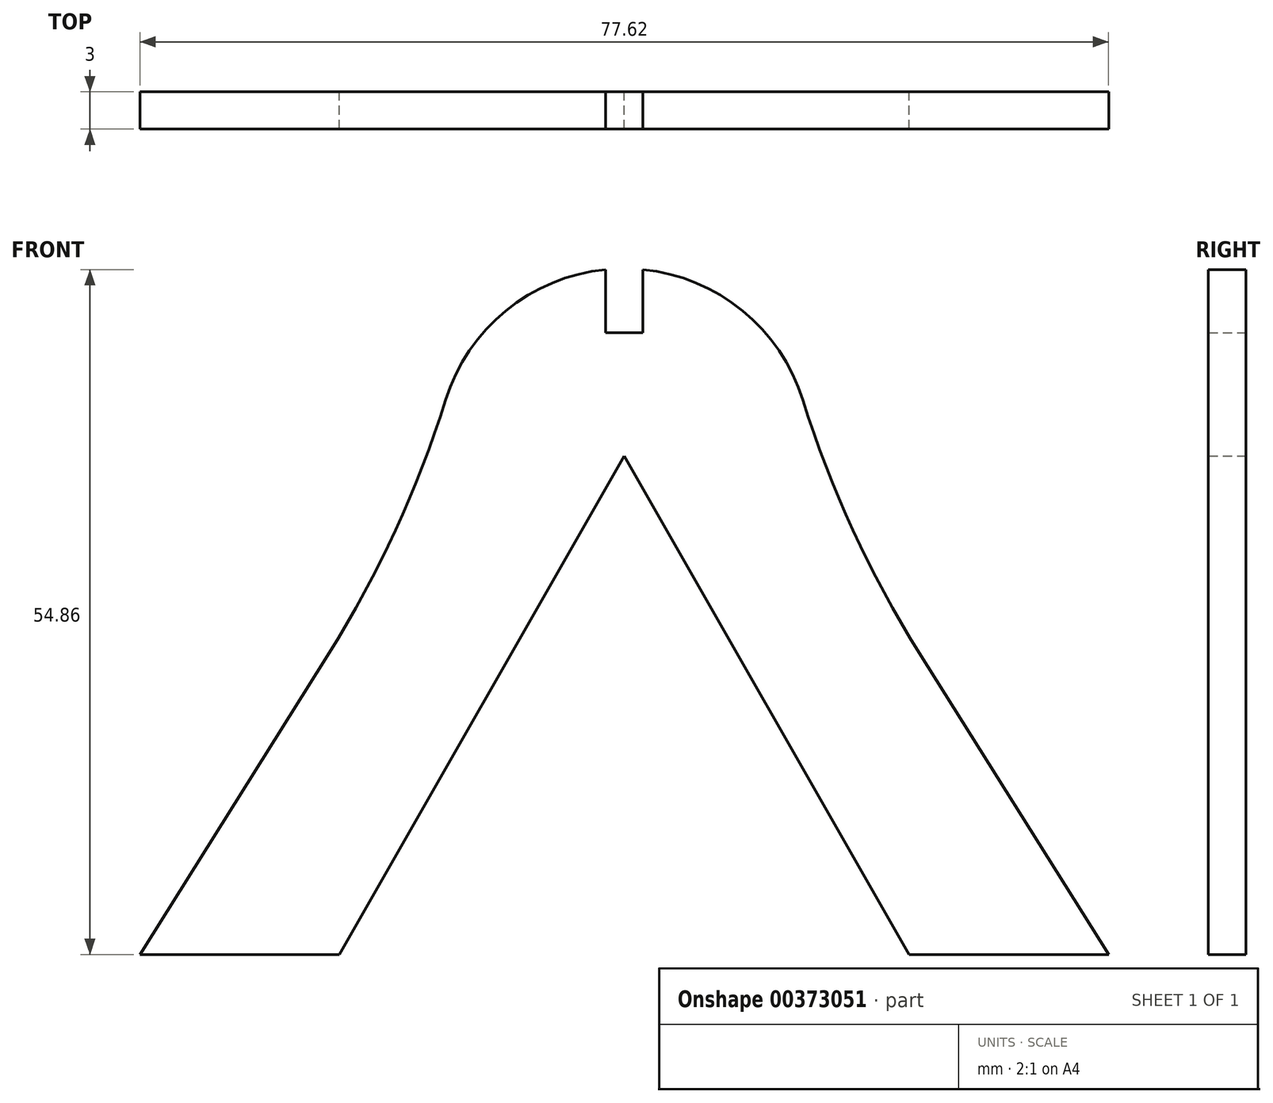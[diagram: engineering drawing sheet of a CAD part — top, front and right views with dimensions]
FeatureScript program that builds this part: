
annotation { "Feature Type Name" : "Feature", "Feature Type Description" : "" }
export const myFeature = defineFeature(function(context is Context, id is Id, definition is map)
    precondition{}
    {
        {
            var Q0;
            Q0=qCreatedBy(makeId("Front.planeOp"),FACE);
            var sketch = newSketch(context, id + "F0", { "sketchPlane" : qUnion([Q0])});
            skLineSegment(sketch, "E0", {"start": v(14.89, -1.83) * mm, "end": v(38.81, -39.94) * mm});
            skLineSegment(sketch, "E1", {"start": v(38.81, -39.94) * mm, "end": v(22.81, -39.94) * mm});
            skLineSegment(sketch, "E2", {"start": v(22.81, -39.94) * mm, "end": v(0, 0) * mm});
            skLineSegment(sketch, "E3.MirrorCS", {"start": v(-14.89, -1.83) * mm, "end": v(-38.81, -39.94) * mm});
            skLineSegment(sketch, "E4.MirrorCS", {"start": v(-38.81, -39.94) * mm, "end": v(-22.81, -39.94) * mm});
            skLineSegment(sketch, "E5.MirrorCS", {"start": v(-22.81, -39.94) * mm, "end": v(0, 0) * mm});
            skArc(sketch, "E6", {"start": v(14.89, -1.83) * mm, "mid": v(11.72, 9.36) * mm, "end": v(1.5, 14.92) * mm});
            skPoint(sketch, "E7.start.orphan", {"position": v(2.46, 0) * mm});
            skPoint(sketch, "E8.MirrorCS.start.orphan", {"position": v(-2.46, 0) * mm});
            skPoint(sketch, "E9.orphan", {"position": v(-13.74, 0) * mm});
            skPoint(sketch, "E10.orphan", {"position": v(13.74, 0) * mm});
            skLineSegment(sketch, "E11.bottom", {"start": v(1.5, 9.86) * mm, "end": v(-1.5, 9.86) * mm});
            skLineSegment(sketch, "E11.left", {"start": v(1.5, 9.86) * mm, "end": v(1.5, 14.92) * mm});
            skLineSegment(sketch, "E11.right", {"start": v(-1.5, 9.86) * mm, "end": v(-1.5, 14.92) * mm});
            skPoint(sketch, "E11.middle", {"position": v(0, 15) * mm});
            skPoint(sketch, "E12.orphan", {"position": v(-1.5, 20.14) * mm});
            skPoint(sketch, "E13.orphan", {"position": v(1.5, 20.14) * mm});
            skArc(sketch, "E14.trimOffspring", {"start": v(-1.5, 14.92) * mm, "mid": v(-11.72, 9.36) * mm, "end": v(-14.89, -1.83) * mm});
            skSolve(sketch);
        }
        {
            var Q0;
            Q0=makeQuery(id+"F0.imprint","IMPRINT",FACE,{"disambiguationData":[TD([[makeQuery(id+"F0.imprint","IMPRINT",EDGE,{"derivedFrom":sQuery(id+"F0.wireOp",EDGE,"E0")}),-1.0]])]});
            extrude(context, id + "F1", {"entities" : qUnion([Q0]), "depth" : 3 * mm});
        }
        {
            var Q0;
            Q0=makeQuery(id+"F1.opExtrude","SWEPT_EDGE",EDGE,{"disambiguationData":[OSD([sQuery(id+"F0.wireOp",EDGE,"E0"),sQuery(id+"F0.wireOp",EDGE,"E6")])]});
            var Q1;
            Q1=makeQuery(id+"F1.opExtrude","SWEPT_EDGE",EDGE,{"disambiguationData":[OSD([sQuery(id+"F0.wireOp",EDGE,"E3.MirrorCS"),sQuery(id+"F0.wireOp",EDGE,"E14.trimOffspring")])]});
            fillet(context, id + "F2", {"entities" : qUnion([Q0, Q1]), "radius" : 86.47 * mm, "tangentPropagation" : true, "allowEdgeOverflow" : false});
        }
    });
